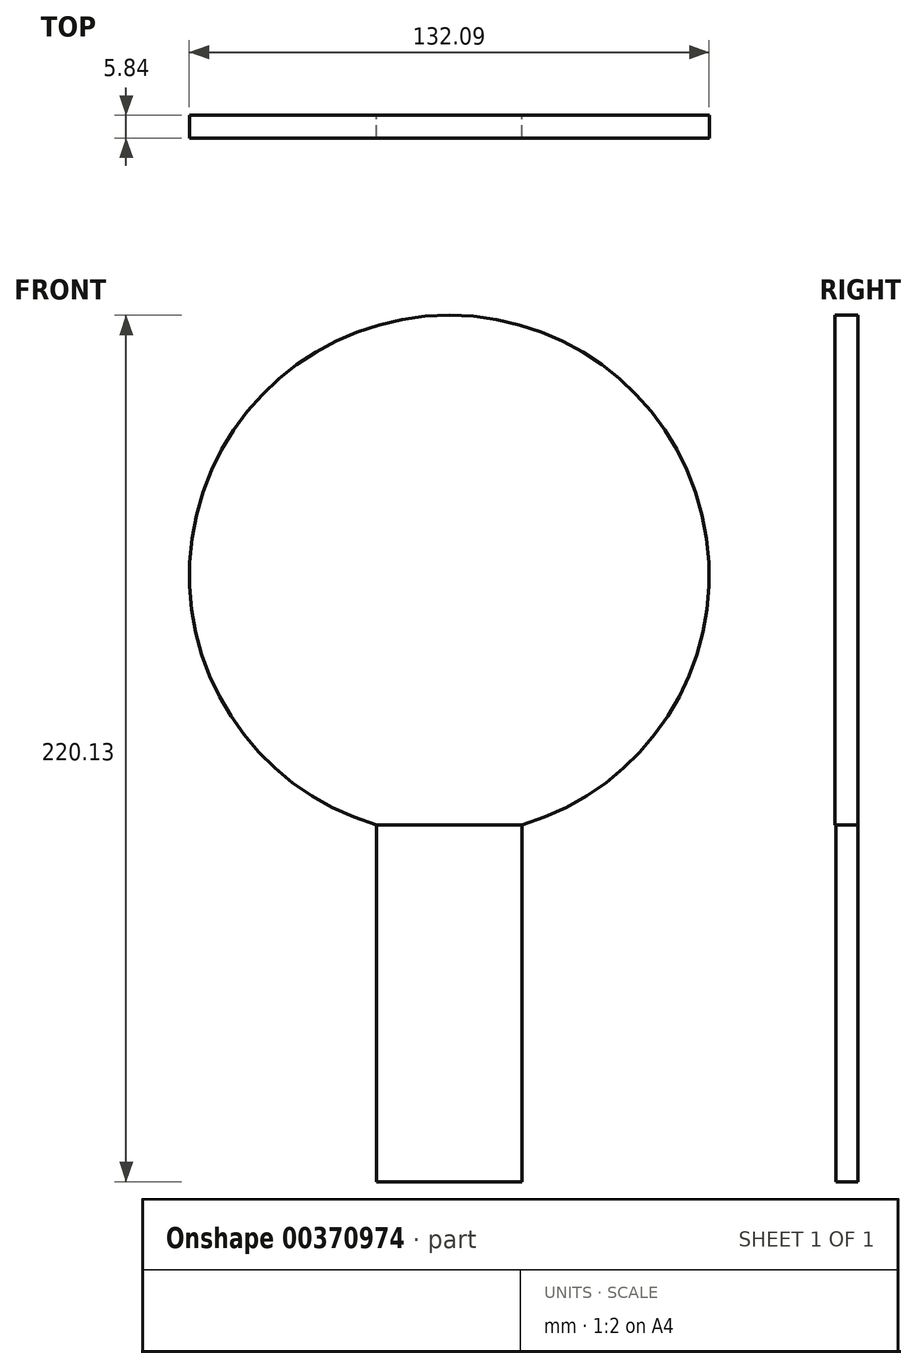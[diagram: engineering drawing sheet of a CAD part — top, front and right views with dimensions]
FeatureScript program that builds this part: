
annotation { "Feature Type Name" : "Feature", "Feature Type Description" : "" }
export const myFeature = defineFeature(function(context is Context, id is Id, definition is map)
    precondition{}
    {
        {
            var Q0;
            Q0=qCreatedBy(makeId("Front.planeOp"),FACE);
            var sketch = newSketch(context, id + "F0", { "sketchPlane" : qUnion([Q0])});
            skArc(sketch, "E0", {"start": v(-17.92, 90.68) * mm, "mid": v(-36.38, 220.13) * mm, "end": v(-54.85, 90.68) * mm});
            skLineSegment(sketch, "E1", {"start": v(-54.85, 90.68) * mm, "end": v(-17.92, 90.68) * mm});
            skLineSegment(sketch, "E2", {"start": v(-17.92, 90.68) * mm, "end": v(-17.92, 0) * mm});
            skLineSegment(sketch, "E3", {"start": v(-17.92, 0) * mm, "end": v(-54.85, 0) * mm});
            skLineSegment(sketch, "E4", {"start": v(-54.85, 0) * mm, "end": v(-54.85, 90.68) * mm});
            skSolve(sketch);
        }
        {
            var Q0;
            Q0=makeQuery(id+"F0.imprint","IMPRINT",FACE,{"disambiguationData":[TD([[makeQuery(id+"F0.imprint","IMPRINT",EDGE,{"derivedFrom":sQuery(id+"F0.wireOp",EDGE,"E0")}),1.0]])]});
            extrude(context, id + "F1", {"entities" : qUnion([Q0]), "depth" : 5.84 * mm});
        }
        {
            var Q0;
            Q0=makeQuery(id+"F0.imprint","IMPRINT",FACE,{"disambiguationData":[TD([[makeQuery(id+"F0.imprint","IMPRINT",EDGE,{"derivedFrom":sQuery(id+"F0.wireOp",EDGE,"E1")}),-1.0]])]});
            extrude(context, id + "F2", {"entities" : qUnion([Q0]), "operationType" : NewBodyOperationType.ADD, "depth" : 5.6 * mm});
        }
    });
